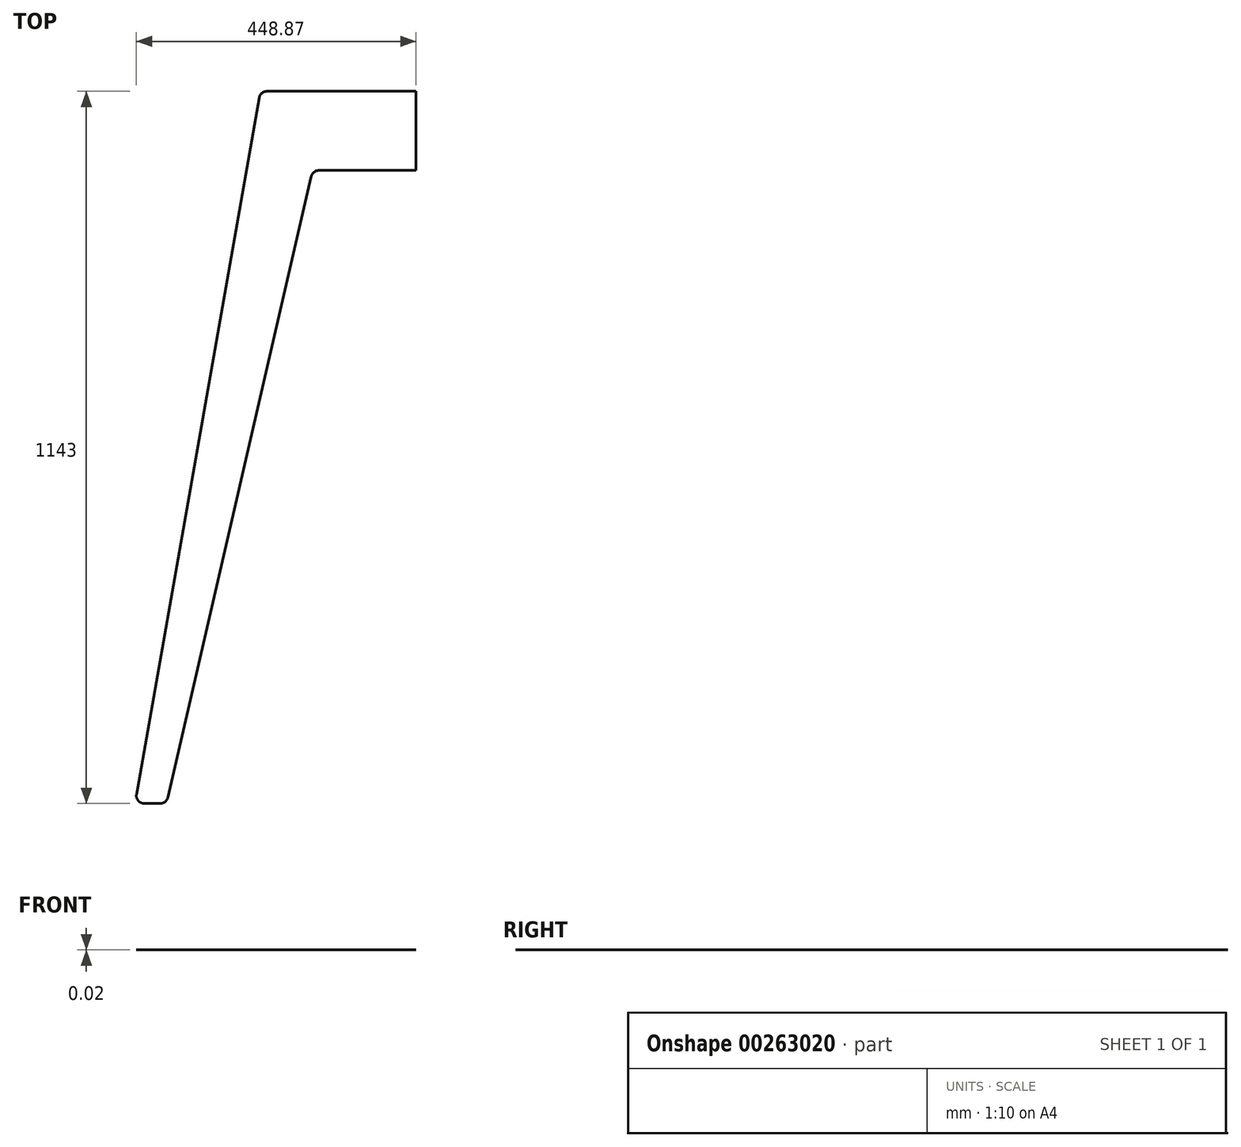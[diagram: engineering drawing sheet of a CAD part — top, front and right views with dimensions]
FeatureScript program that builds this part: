
annotation { "Feature Type Name" : "Feature", "Feature Type Description" : "" }
export const myFeature = defineFeature(function(context is Context, id is Id, definition is map)
    precondition{}
    {
        {
            var Q0;
            Q0=qCreatedBy(makeId("Top.planeOp"),FACE);
            var sketch = newSketch(context, id + "F0", { "sketchPlane" : qUnion([Q0])});
            skLineSegment(sketch, "E0", {"start": v(0, 0) * mm, "end": v(50.8, 0) * mm});
            skLineSegment(sketch, "E1", {"start": v(50.8, 0) * mm, "end": v(285.36, 1016) * mm});
            skLineSegment(sketch, "E2", {"start": v(285.36, 1016) * mm, "end": v(451.3, 1016) * mm});
            skLineSegment(sketch, "E3", {"start": v(451.3, 1016) * mm, "end": v(451.3, 1143) * mm});
            skLineSegment(sketch, "E4", {"start": v(451.3, 1143) * mm, "end": v(201.54, 1143) * mm});
            skLineSegment(sketch, "E5", {"start": v(201.54, 1143) * mm, "end": v(0, 0) * mm});
            skSolve(sketch);
        }
        {
            var Q0;
            Q0=makeQuery(id+"F0.imprint","IMPRINT",FACE,{"disambiguationData":[TD([[makeQuery(id+"F0.imprint","IMPRINT",EDGE,{"derivedFrom":sQuery(id+"F0.wireOp",EDGE,"E0")}),1.0]])]});
            extrude(context, id + "F1", {"entities" : qUnion([Q0]), "depth" : 5 / 203.2 * mm, "offsetDistance" : 25 * mm});
        }
        {
            var Q0;
            Q0=makeQuery(id+"F1.opExtrude","SWEPT_EDGE",EDGE,{"disambiguationData":[OSD([sQuery(id+"F0.wireOp",EDGE,"E4"),sQuery(id+"F0.wireOp",EDGE,"E5")])]});
            var Q1;
            Q1=makeQuery(id+"F1.opExtrude","SWEPT_EDGE",EDGE,{"disambiguationData":[OSD([sQuery(id+"F0.wireOp",EDGE,"E1"),sQuery(id+"F0.wireOp",EDGE,"E2")])]});
            var Q2;
            Q2=makeQuery(id+"F1.opExtrude","SWEPT_EDGE",EDGE,{"disambiguationData":[OSD([sQuery(id+"F0.wireOp",EDGE,"E0"),sQuery(id+"F0.wireOp",EDGE,"E5")])]});
            var Q3;
            Q3=makeQuery(id+"F1.opExtrude","SWEPT_EDGE",EDGE,{"disambiguationData":[OSD([sQuery(id+"F0.wireOp",EDGE,"E0"),sQuery(id+"F0.wireOp",EDGE,"E1")])]});
            fillet(context, id + "F2", {"entities" : qUnion([Q0, Q1, Q2, Q3]), "radius" : 12.7 * mm, "tangentPropagation" : true, "allowEdgeOverflow" : false});
        }
    });
